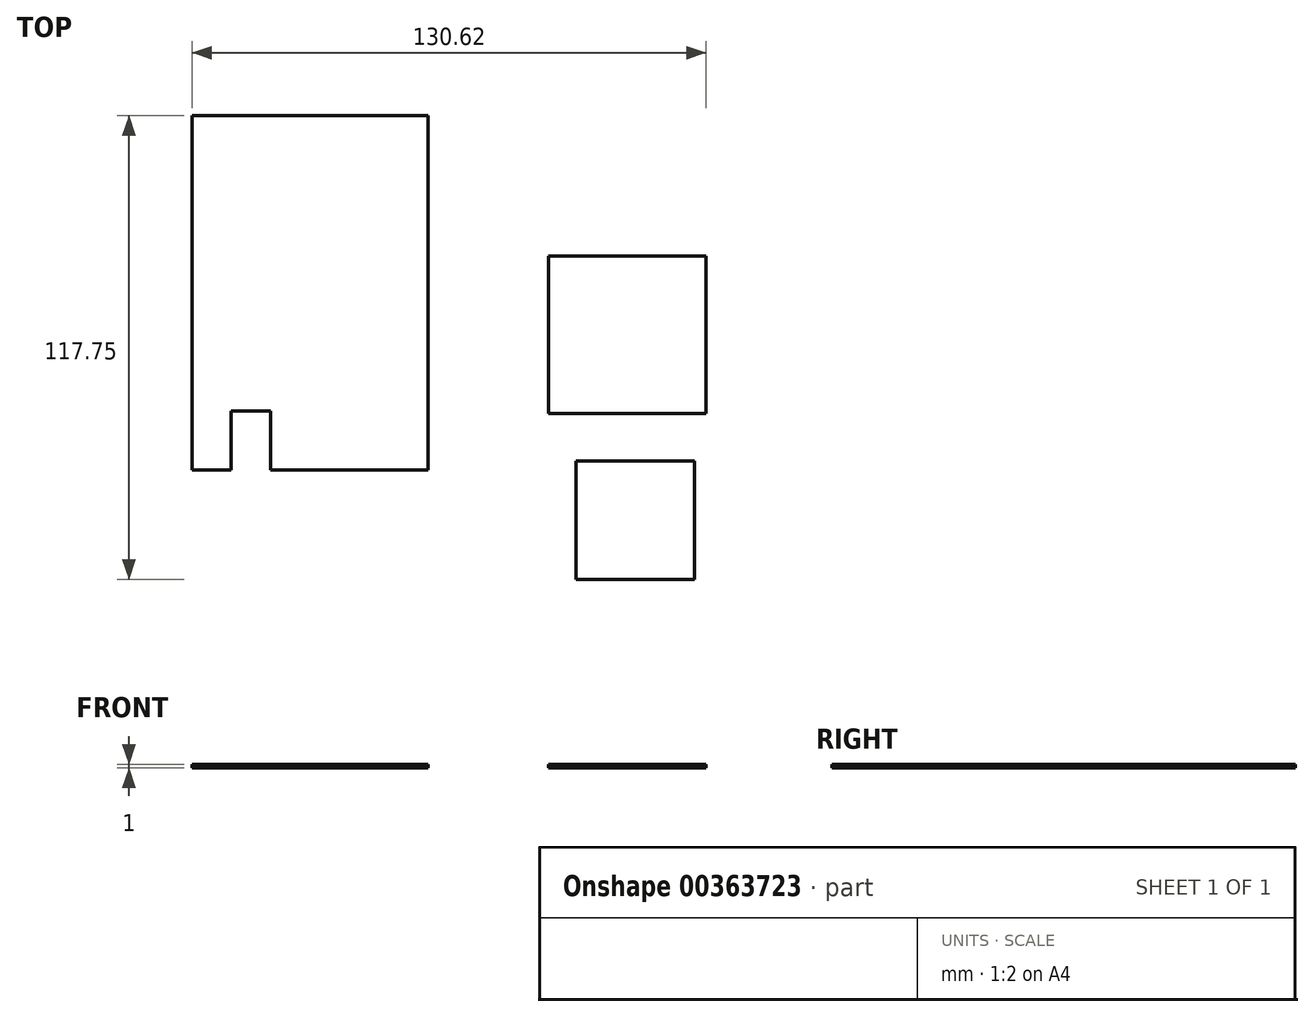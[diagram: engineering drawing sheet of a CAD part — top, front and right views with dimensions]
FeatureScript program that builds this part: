
annotation { "Feature Type Name" : "Feature", "Feature Type Description" : "" }
export const myFeature = defineFeature(function(context is Context, id is Id, definition is map)
    precondition{}
    {
        {
            var Q0;
            Q0=qCreatedBy(makeId("Top.planeOp"),FACE);
            var sketch = newSketch(context, id + "F0", { "sketchPlane" : qUnion([Q0])});
            skLineSegment(sketch, "E0.bottom", {"start": v(-65, 95) * mm, "end": v(-5, 95) * mm});
            skLineSegment(sketch, "E0.top", {"start": v(-65, 5) * mm, "end": v(-5, 5) * mm});
            skLineSegment(sketch, "E0.left", {"start": v(-65, 95) * mm, "end": v(-65, 5) * mm});
            skLineSegment(sketch, "E0.right", {"start": v(-5, 95) * mm, "end": v(-5, 5) * mm});
            skLineSegment(sketch, "E1.bottom", {"start": v(-55, 5) * mm, "end": v(-45, 5) * mm});
            skLineSegment(sketch, "E1.top", {"start": v(-55, 20) * mm, "end": v(-45, 20) * mm});
            skLineSegment(sketch, "E1.left", {"start": v(-55, 5) * mm, "end": v(-55, 20) * mm});
            skLineSegment(sketch, "E1.right", {"start": v(-45, 5) * mm, "end": v(-45, 20) * mm});
            skSolve(sketch);
        }
        {
            var Q0;
            Q0=makeQuery(id+"F0.imprint","IMPRINT",FACE,{"disambiguationData":[TD([[makeQuery(id+"F0.imprint","IMPRINT",EDGE,{"derivedFrom":sQuery(id+"F0.wireOp",EDGE,"E0.bottom")}),-1.0]])]});
            extrude(context, id + "F1", {"entities" : qUnion([Q0]), "depth" : 1 * mm, "offsetDistance" : 25 * mm});
        }
        {
            var Q0;
            Q0=qCreatedBy(makeId("Top.planeOp"),FACE);
            var sketch = newSketch(context, id + "F2", { "sketchPlane" : qUnion([Q0])});
            skLineSegment(sketch, "E2.bottom", {"start": v(25.62, 59.32) * mm, "end": v(65.62, 59.32) * mm});
            skLineSegment(sketch, "E2.top", {"start": v(25.62, 19.32) * mm, "end": v(65.62, 19.32) * mm});
            skLineSegment(sketch, "E2.left", {"start": v(25.62, 59.32) * mm, "end": v(25.62, 19.32) * mm});
            skLineSegment(sketch, "E2.right", {"start": v(65.62, 59.32) * mm, "end": v(65.62, 19.32) * mm});
            skLineSegment(sketch, "E3.bottom", {"start": v(32.63, 7.25) * mm, "end": v(62.63, 7.25) * mm});
            skLineSegment(sketch, "E3.top", {"start": v(32.63, -22.75) * mm, "end": v(62.63, -22.75) * mm});
            skLineSegment(sketch, "E3.left", {"start": v(32.63, 7.25) * mm, "end": v(32.63, -22.75) * mm});
            skLineSegment(sketch, "E3.right", {"start": v(62.63, 7.25) * mm, "end": v(62.63, -22.75) * mm});
            skSolve(sketch);
        }
        {
            var Q0;
            Q0=makeQuery(id+"F2.imprint","IMPRINT",FACE,{"disambiguationData":[TD([[makeQuery(id+"F2.imprint","IMPRINT",EDGE,{"derivedFrom":sQuery(id+"F2.wireOp",EDGE,"E2.bottom")}),-1.0]])]});
            var Q1;
            Q1=makeQuery(id+"F2.imprint","IMPRINT",FACE,{"disambiguationData":[TD([[makeQuery(id+"F2.imprint","IMPRINT",EDGE,{"derivedFrom":sQuery(id+"F2.wireOp",EDGE,"E3.bottom")}),-1.0]])]});
            extrude(context, id + "F3", {"entities" : qUnion([Q0, Q1]), "depth" : 1 * mm, "offsetDistance" : 25 * mm});
        }
    });
